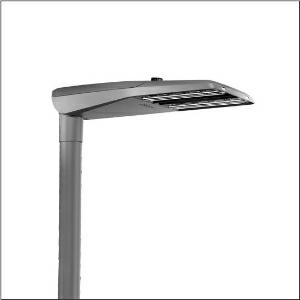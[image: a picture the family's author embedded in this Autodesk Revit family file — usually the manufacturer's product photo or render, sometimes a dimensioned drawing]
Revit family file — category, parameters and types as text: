
# Revit family: streetlight_sl_11_iq_midi___st1_2a_5xc3a41u08le_6743
name_source: partatom
category: Lighting Fixtures
units: mm (PartAtom-declared; Revit-internal decimal feet)

## family parameters
Cut with Voids When Loaded = No
Host = Face
Light Source = No
Part Type = Normal
Room Calculation Point = No
Round Connector Dimension = Use Diameter
Shared = No

## types (1)
- --- (1 x LED, 9590 lm, 59.4 W, 4000K)
    Apparent Load = 59 VA
    CIE Flux Codes = 32 70 96 100 100
    Color Rendering = 70
    Color Temperature = 4000K
    Default Elevation = 1800 mm
    Description = Streetlight SL 11 iQ midi, mast luminaire, primary light control with 3 zone facetted reflector, of plastic, silver coated, highly specular, primary optical cover: cover, of PMMA, transparent, light distribution: ST1.2a, light emission: direct distribution, primary light characteristic: asymmetric, installation type: post-top, side-entry, LED, High Power LED, rated luminous flux: 9.590lm, luminous efficacy: 163lm/W, light colour: 740, colour temperature: 4000K, control: presetting dimming logarithmic, Street-Remote, Auto-Match, Temp-Guard, Lumen-Switch, Night-Set, Smart-Wire, Light-Fading, Desk-Remote (wireless, voltage-free reading and setting of iQ features in the workshop via application-optimized NFC function/RFID function), optimised constant luminous flux control (CLO 2.0), with cable H07RN-F 5x 1.5mm², mains connection: 220..240V, AC, 50/60Hz, connection cable pre-assembled, cable length: 8,5m, start of lifetime: 59W, end of service life: 62W, reduction: 29W, luminaire housing, of diecast aluminium, powder-coated, Siteco® metallic grey (DB 702S), please order mast flange separately, inclination adjustable without tools: 0°, 5°, 10°, 15° (post-top) | 0°, -5°, -10°, -15° (side-entry), sealing non-destructively replaceable, multi-level sealing system, length: 780mm, width: 376mm, height: 118mm, spigot size: 60/76mm (post-top) and 42/60/76mm (side-entry), mast flange for spigot size: 42mm: 5XC10008XM4, 60mm: 5XC10008XM2, 76/60mm: 5XC10108XM1, equipment: standard, Smart Interface below, protection rating (complete): IP66, insulation class (complete): insulation class II (safety insulation), certification: CE, ENEC in preparation, impact resistance: IK09, permissible operating ambient temperature for outdoor applications: -25..+50°C, standard-compliant lighting for roads and squares, packaging unit: 1 piece

Light Distribution: ST1.2a
    Height = 118 mm
    Lamp = 1 x LED
    Lamp Light Flux = 9590 lm
    Lamp Power = 59.4 W
    Lamp count = 1
    Length = 780 mm
    Luminous efficacy = 161 lm/W
    Manufacturer = Siteco
    ModVariant = No
    Model = 5XC3A41U08LE
    Number of Poles = 1
    OnlyDefault = Yes
    Power Factor = 1
    Product Name = Streetlight SL 11 iQ midi | ST1.2a
    Product group = mast luminaire | pylon top
    ProductGroupID = 6100
    Protection Class = Protection class II
    Protection Degree = IP 66
    RLX_Detail_Level = 1
    RlxData = <blob elided: 69545 chars, md5=0e866596>
    Socket = socket
    Standby Power = 0 W
    System Light Flux = 9590 lm
    System Power = 59 W
    Type Comments = factory setting: luminous flux: 100 % | dim-lin: 254 | 521 mA
    Type Image = l_1005968.jpg
    URL = http://relux.com
    VarID = @adj_043543
    Voltage = 0 V
    Weight = 0.00 kg
    Width = 376 mm

## geometry (parser evidence)
native form markers: Blend x4, Sweep x8
no freeform markers — native parametric forms only
